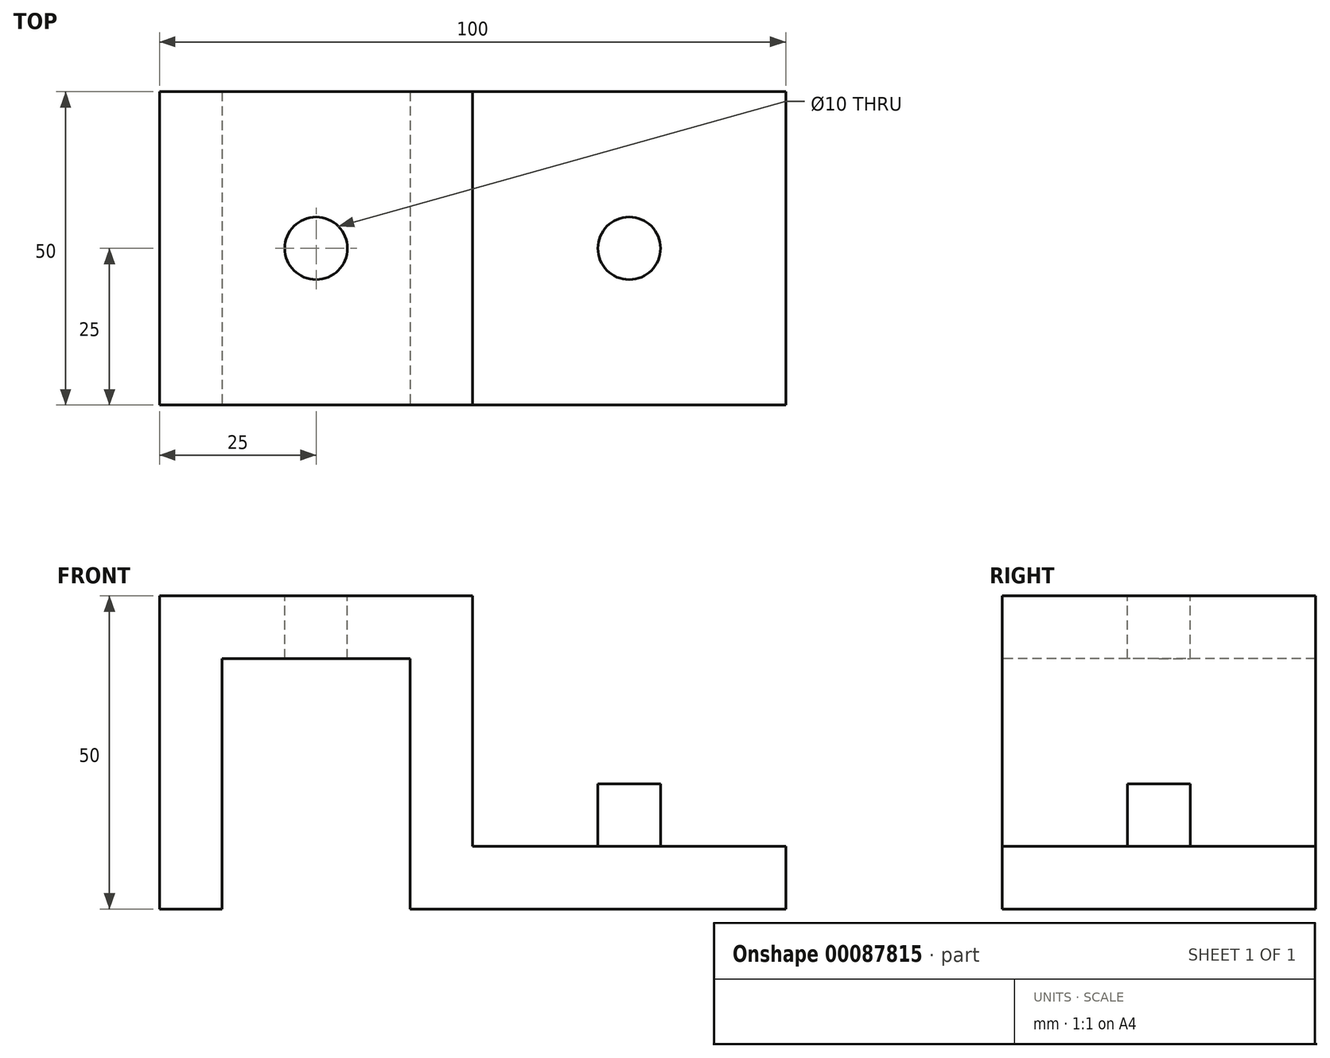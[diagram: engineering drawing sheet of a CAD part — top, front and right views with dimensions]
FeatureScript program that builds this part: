
annotation { "Feature Type Name" : "Feature", "Feature Type Description" : "" }
export const myFeature = defineFeature(function(context is Context, id is Id, definition is map)
    precondition{}
    {
        {
            var Q0;
            Q0=qCreatedBy(makeId("Front.planeOp"),FACE);
            var sketch = newSketch(context, id + "F0", { "sketchPlane" : qUnion([Q0])});
            skLineSegment(sketch, "E0", {"start": v(0, 0) * mm, "end": v(0, 50) * mm});
            skLineSegment(sketch, "E1", {"start": v(0, 50) * mm, "end": v(50, 50) * mm});
            skLineSegment(sketch, "E2", {"start": v(50, 50) * mm, "end": v(50, 10) * mm});
            skLineSegment(sketch, "E3", {"start": v(50, 10) * mm, "end": v(100, 10) * mm});
            skLineSegment(sketch, "E4", {"start": v(100, 10) * mm, "end": v(100, 0) * mm});
            skLineSegment(sketch, "E5", {"start": v(100, 0) * mm, "end": v(0, 0) * mm});
            skSolve(sketch);
        }
        {
            var Q0;
            Q0 = qSketchRegion(id + "F0", true);
            extrude(context, id + "F1", {"entities" : qUnion([Q0]), "depth" : 50 * mm});
        }
        {
            var Q0;
            Q0=makeQuery(id+"F1.opExtrude","CAP_FACE",FACE,{"disambiguationData":[OSD([sQuery(id+"F0.wireOp",EDGE,"E0"),sQuery(id+"F0.wireOp",EDGE,"E1"),sQuery(id+"F0.wireOp",EDGE,"E2"),sQuery(id+"F0.wireOp",EDGE,"E3"),sQuery(id+"F0.wireOp",EDGE,"E4"),sQuery(id+"F0.wireOp",EDGE,"E5")])],"isStart":false});
            var sketch = newSketch(context, id + "F2", { "sketchPlane" : qUnion([Q0])});
            skLineSegment(sketch, "E6.bottom", {"start": v(10, 0) * mm, "end": v(40, 0) * mm});
            skLineSegment(sketch, "E6.top", {"start": v(10, 40) * mm, "end": v(40, 40) * mm});
            skLineSegment(sketch, "E6.left", {"start": v(10, 0) * mm, "end": v(10, 40) * mm});
            skLineSegment(sketch, "E6.right", {"start": v(40, 0) * mm, "end": v(40, 40) * mm});
            skSolve(sketch);
        }
        {
            var Q0;
            Q0 = qSketchRegion(id + "F2", true);
            extrude(context, id + "F3", {"entities" : qUnion([Q0]), "operationType" : NewBodyOperationType.REMOVE, "endBound" : BoundingType.THROUGH_ALL, "oppositeDirection" : true, "depth" : 25 * mm});
        }
        {
            var Q0;
            Q0=makeQuery(id+"F1.opExtrude","SWEPT_FACE",FACE,{"disambiguationData":[OSD([sQuery(id+"F0.wireOp",EDGE,"E1")])]});
            var sketch = newSketch(context, id + "F4", { "sketchPlane" : qUnion([Q0])});
            skCircle(sketch, "E7", {"center": v(25, -25) * mm, "radius": 5 * mm});
            skSolve(sketch);
        }
        {
            var Q0;
            Q0 = qSketchRegion(id + "F4", true);
            extrude(context, id + "F5", {"entities" : qUnion([Q0]), "operationType" : NewBodyOperationType.REMOVE, "endBound" : BoundingType.THROUGH_ALL, "oppositeDirection" : true, "depth" : 25 * mm});
        }
        {
            var Q0;
            Q0=makeQuery(id+"F1.opExtrude","SWEPT_FACE",FACE,{"disambiguationData":[OSD([sQuery(id+"F0.wireOp",EDGE,"E3")])]});
            var sketch = newSketch(context, id + "F6", { "sketchPlane" : qUnion([Q0])});
            skCircle(sketch, "E8", {"center": v(75, -25) * mm, "radius": 5 * mm});
            skSolve(sketch);
        }
        {
            var Q0;
            Q0 = qSketchRegion(id + "F6", true);
            extrude(context, id + "F7", {"entities" : qUnion([Q0]), "operationType" : NewBodyOperationType.ADD, "depth" : 10 * mm});
        }
    });
